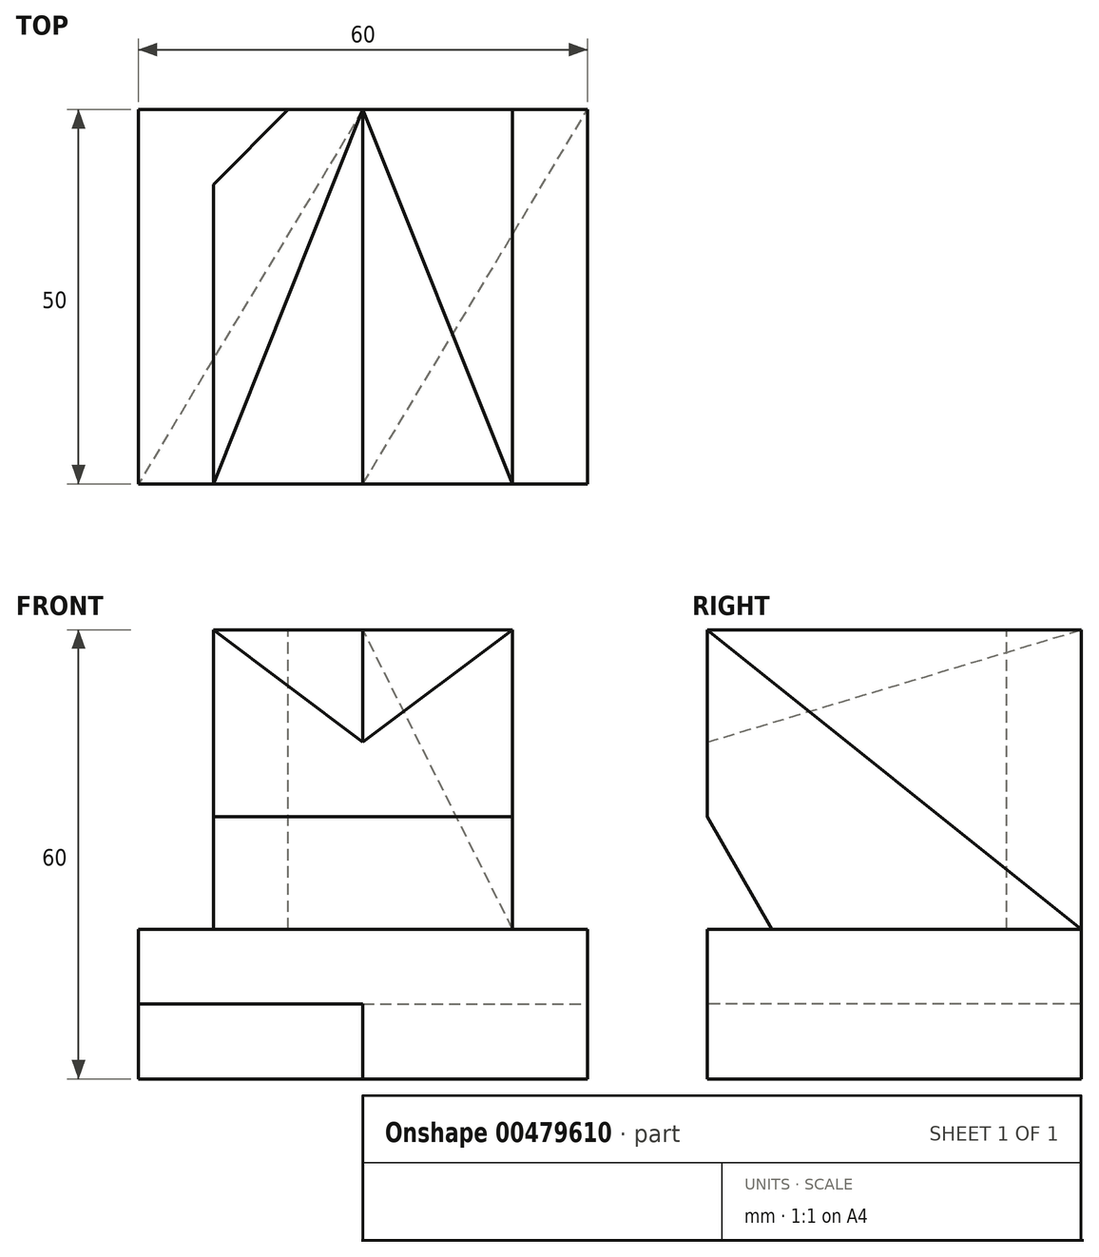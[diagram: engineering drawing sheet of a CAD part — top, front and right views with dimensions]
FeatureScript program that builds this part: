
annotation { "Feature Type Name" : "Feature", "Feature Type Description" : "" }
export const myFeature = defineFeature(function(context is Context, id is Id, definition is map)
    precondition{}
    {
        {
            var Q0;
            Q0=qCreatedBy(makeId("Top.planeOp"),FACE);
            var sketch = newSketch(context, id + "F0", { "sketchPlane" : qUnion([Q0])});
            skLineSegment(sketch, "E0.bottom", {"start": v(0, 0) * mm, "end": v(60, 0) * mm});
            skLineSegment(sketch, "E0.top", {"start": v(0, 50) * mm, "end": v(60, 50) * mm});
            skLineSegment(sketch, "E0.left", {"start": v(0, 0) * mm, "end": v(0, 50) * mm});
            skLineSegment(sketch, "E0.right", {"start": v(60, 0) * mm, "end": v(60, 50) * mm});
            skSolve(sketch);
        }
        {
            var Q0;
            Q0 = qSketchRegion(id + "F0", true);
            extrude(context, id + "F1", {"entities" : qUnion([Q0]), "depth" : 60 * mm});
        }
        {
            var Q0;
            Q0=makeQuery(id+"F1.opExtrude","CAP_FACE",FACE,{"disambiguationData":[OSD([sQuery(id+"F0.wireOp",EDGE,"E0.bottom"),sQuery(id+"F0.wireOp",EDGE,"E0.top"),sQuery(id+"F0.wireOp",EDGE,"E0.left"),sQuery(id+"F0.wireOp",EDGE,"E0.right")])],"isStart":false});
            var sketch = newSketch(context, id + "F2", { "sketchPlane" : qUnion([Q0])});
            skLineSegment(sketch, "E1.bottom", {"start": v(0, 0) * mm, "end": v(10, 0) * mm});
            skLineSegment(sketch, "E1.top", {"start": v(0, 50) * mm, "end": v(10, 50) * mm});
            skLineSegment(sketch, "E1.left", {"start": v(0, 0) * mm, "end": v(0, 50) * mm});
            skLineSegment(sketch, "E1.right", {"start": v(10, 0) * mm, "end": v(10, 50) * mm});
            skLineSegment(sketch, "E2.bottom", {"start": v(60, 0) * mm, "end": v(50, 0) * mm});
            skLineSegment(sketch, "E2.top", {"start": v(60, 50) * mm, "end": v(50, 50) * mm});
            skLineSegment(sketch, "E2.left", {"start": v(60, 0) * mm, "end": v(60, 50) * mm});
            skLineSegment(sketch, "E2.right", {"start": v(50, 0) * mm, "end": v(50, 50) * mm});
            skLineSegment(sketch, "E3", {"start": v(10, 50) * mm, "end": v(20, 50) * mm});
            skLineSegment(sketch, "E4", {"start": v(20, 50) * mm, "end": v(10, 40) * mm});
            skLineSegment(sketch, "E5", {"start": v(10, 40) * mm, "end": v(10, 50) * mm});
            skSolve(sketch);
        }
        {
            var Q0;
            Q0=makeQuery(id+"F2.imprint","IMPRINT",FACE,{"disambiguationData":[TD([[makeQuery(id+"F2.imprint","IMPRINT",EDGE,{"derivedFrom":sQuery(id+"F2.wireOp",EDGE,"E1.bottom")}),1.0]])]});
            var Q1;
            Q1=makeQuery(id+"F2.imprint","IMPRINT",FACE,{"disambiguationData":[TD([[makeQuery(id+"F2.imprint","IMPRINT",EDGE,{"derivedFrom":sQuery(id+"F2.wireOp",EDGE,"E2.bottom")}),1.0]])]});
            var Q2;
            Q2=makeQuery(id+"F2.imprint","IMPRINT",FACE,{"disambiguationData":[TD([[makeQuery(id+"F2.imprint","IMPRINT",EDGE,{"derivedFrom":sQuery(id+"F2.wireOp",EDGE,"E3")}),-1.0]])]});
            extrude(context, id + "F3", {"entities" : qUnion([Q0, Q1, Q2]), "operationType" : NewBodyOperationType.REMOVE, "oppositeDirection" : true, "depth" : 40 * mm});
        }
        {
            var Q0;
            Q0=makeQuery(id+"F1.opExtrude","CAP_FACE",FACE,{"disambiguationData":[OSD([sQuery(id+"F0.wireOp",EDGE,"E0.bottom"),sQuery(id+"F0.wireOp",EDGE,"E0.top"),sQuery(id+"F0.wireOp",EDGE,"E0.left"),sQuery(id+"F0.wireOp",EDGE,"E0.right")])],"isStart":true});
            var sketch = newSketch(context, id + "F4", { "sketchPlane" : qUnion([Q0])});
            skLineSegment(sketch, "E6", {"start": v(60, -50) * mm, "end": v(30, -50) * mm});
            skLineSegment(sketch, "E7", {"start": v(30, -50) * mm, "end": v(0, 0) * mm});
            skLineSegment(sketch, "E8", {"start": v(0, 0) * mm, "end": v(30, 0) * mm});
            skLineSegment(sketch, "E9", {"start": v(30, 0) * mm, "end": v(60, -50) * mm});
            skSolve(sketch);
        }
        {
            var Q0;
            Q0=makeQuery(id+"F4.imprint","IMPRINT",FACE,{"disambiguationData":[TD([[makeQuery(id+"F4.imprint","IMPRINT",EDGE,{"derivedFrom":sQuery(id+"F4.wireOp",EDGE,"E6")}),1.0]])]});
            extrude(context, id + "F5", {"entities" : qUnion([Q0]), "operationType" : NewBodyOperationType.REMOVE, "oppositeDirection" : true, "depth" : 10 * mm, "offsetDistance" : 25 * mm});
        }
        {
            var Q0;
            Q0=makeQuery(id+"F1.opExtrude","SWEPT_FACE",FACE,{"disambiguationData":[OSD([sQuery(id+"F0.wireOp",EDGE,"E0.bottom")])]});
            var sketch = newSketch(context, id + "F6", { "sketchPlane" : qUnion([Q0])});
            skLineSegment(sketch, "E10", {"start": v(50, 60) * mm, "end": v(30, 45) * mm});
            skLineSegment(sketch, "E11", {"start": v(30, 45) * mm, "end": v(10, 60) * mm});
            skSolve(sketch);
        }
        {
            var Q0;
            Q0=makeQuery(id+"F3.boolean.opBoolean","COPY",FACE,{"derivedFrom":makeQuery(id+"F3.opExtrude","SWEPT_FACE",FACE,{"disambiguationData":[OSD([sQuery(id+"F2.wireOp",EDGE,"E2.right")])]})});
            var sketch = newSketch(context, id + "F7", { "sketchPlane" : qUnion([Q0])});
            skLineSegment(sketch, "E12", {"start": v(0, 45) * mm, "end": v(50, 60) * mm});
            skSolve(sketch);
        }
        {
            var Q0;
            Q0=makeQuery(id+"F6.imprint","IMPRINT",FACE,{"disambiguationData":[TD([[makeQuery(id+"F6.imprint","IMPRINT",EDGE,{"derivedFrom":sQuery(id+"F6.wireOp",EDGE,"E10")}),-1.0]])]});
            var Q1;
            Q1=sQuery(id+"F7.wireOp",EDGE,"E12");
            sweep(context, id + "F8", {"operationType" : NewBodyOperationType.REMOVE, "profiles" : qUnion([Q0]), "path" : qUnion([Q1])});
        }
        {
            var Q0;
            Q0=makeQuery(id+"F3.boolean.opBoolean","COPY",FACE,{"derivedFrom":makeQuery(id+"F3.opExtrude","SWEPT_FACE",FACE,{"disambiguationData":[OSD([sQuery(id+"F2.wireOp",EDGE,"E2.right")])]})});
            var sketch = newSketch(context, id + "F9", { "sketchPlane" : qUnion([Q0])});
            skLineSegment(sketch, "E13", {"start": v(0, 20) * mm, "end": v(0, 35) * mm});
            skLineSegment(sketch, "E14", {"start": v(0, 35) * mm, "end": v(8.66, 20) * mm});
            skLineSegment(sketch, "E15", {"start": v(8.66, 20) * mm, "end": v(0, 20) * mm});
            skSolve(sketch);
        }
        {
            var Q0;
            Q0=makeQuery(id+"F9.imprint","IMPRINT",FACE,{"disambiguationData":[TD([[makeQuery(id+"F9.imprint","IMPRINT",EDGE,{"derivedFrom":sQuery(id+"F9.wireOp",EDGE,"E13")}),-1.0]])]});
            extrude(context, id + "F10", {"entities" : qUnion([Q0]), "operationType" : NewBodyOperationType.REMOVE, "endBound" : BoundingType.THROUGH_ALL, "oppositeDirection" : true, "depth" : 25 * mm, "offsetDistance" : 25 * mm});
        }
        {
            var Q0;
            Q0=makeQuery(id+"F3.boolean.opBoolean","COPY",FACE,{"derivedFrom":makeQuery(id+"F3.opExtrude","SWEPT_FACE",FACE,{"disambiguationData":[OSD([sQuery(id+"F2.wireOp",EDGE,"E2.right")])]})});
            var sketch = newSketch(context, id + "F11", { "sketchPlane" : qUnion([Q0])});
            skLineSegment(sketch, "E16", {"start": v(50, 20) * mm, "end": v(0, 60) * mm});
            skSolve(sketch);
        }
        {
            var Q0;
            Q0=makeQuery(id+"F1.opExtrude","SWEPT_FACE",FACE,{"disambiguationData":[OSD([sQuery(id+"F0.wireOp",EDGE,"E0.top")])]});
            var sketch = newSketch(context, id + "F12", { "sketchPlane" : qUnion([Q0])});
            skLineSegment(sketch, "E17", {"start": v(-50, 20) * mm, "end": v(-30, 60) * mm});
            skSolve(sketch);
        }
        {
            var Q0;
            Q0=makeQuery(id+"F11.imprint","IMPRINT",FACE,{"disambiguationData":[TD([[makeQuery(id+"F11.imprint","IMPRINT",EDGE,{"derivedFrom":sQuery(id+"F11.wireOp",EDGE,"E16")}),-1.0]])]});
            var Q1;
            Q1=sQuery(id+"F12.wireOp",EDGE,"E17");
            sweep(context, id + "F13", {"operationType" : NewBodyOperationType.REMOVE, "profiles" : qUnion([Q0]), "path" : qUnion([Q1])});
        }
    });
